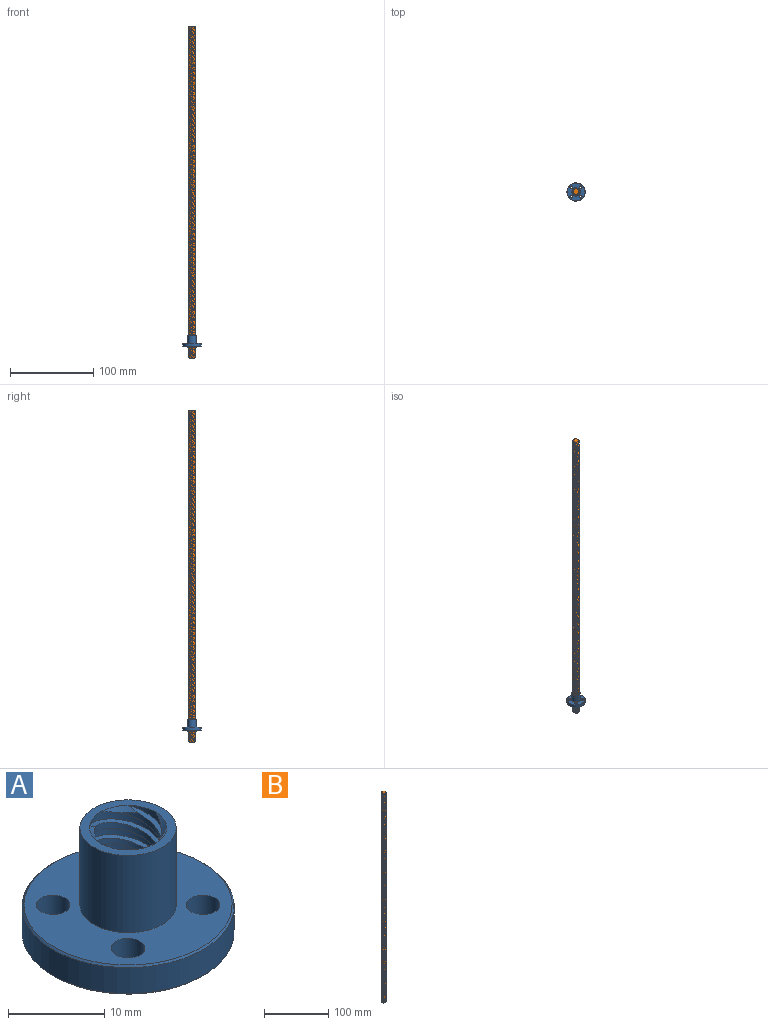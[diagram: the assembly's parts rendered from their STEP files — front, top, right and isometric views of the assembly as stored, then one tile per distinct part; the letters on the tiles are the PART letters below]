
ASSEMBLY  parts=2 mates=1
PART A: 37 faces, bbox 22x22x17.5 mm
  f0: plane 10x10mm, normal (0,0,-1), area 28.3mm2, adj f9,f11,f15,f19,f23,f29,f30,f31
  f1: plane 10x10mm, normal (0,0,1), area 28.3mm2, adj f10,f11,f15,f19,f23,f33,f34,f35
  f2: cylinder r=1.75mm len=3.7mm, axis (0,0,-1), area 40.7mm2, adj f7,f8
  f3: cylinder r=1.75mm len=3.7mm, axis (0,0,-1), area 40.7mm2, adj f7,f8
  f4: cylinder r=1.75mm len=3.7mm, axis (0,0,-1), area 40.7mm2, adj f7,f8
  f5: cylinder r=1.75mm len=3.7mm, axis (0,0,-1), area 40.7mm2, adj f7,f8
  f6: cylinder r=11mm len=22mm, axis (0,0,-1), area 228.1mm2, adj f27,f28
  f7: plane 21.6x21.6mm, normal (0,0,1), area 249.4mm2, adj f2,f3,f4,f5,f10,f28
  f8: plane 21.6x21.6mm, normal (0,0,-1), area 249.4mm2, adj f2,f3,f4,f5,f9,f27
  f9: cylinder r=5mm len=10mm, axis (0,0,-1), area 47.1mm2, adj f0,f8
  f10: cylinder r=5mm len=10mm, axis (0,0,-1), area 307.9mm2, adj f1,f7
  f11: cylinder r=4mm len=15mm, axis (0,0,-1), area 47.1mm2, adj f0,f1,f14,f26
  f12: bspline ~16.4x9mm, area 23.4mm2, adj f13,f15,f30,f36
  f13: cylinder r=3.5mm len=14mm, axis (0,0,1), area 28.2mm2, adj f12,f14,f30,f36
  f14: bspline ~17.4x9mm, area 23.4mm2, adj f11,f13,f30,f36
  f15: cylinder r=4mm len=15mm, axis (0,0,-1), area 47.1mm2, adj f0,f1,f12,f18
  f16: bspline ~16.4x9mm, area 23.4mm2, adj f17,f19,f29,f35
  f17: cylinder r=3.5mm len=14mm, axis (0,0,1), area 28.2mm2, adj f16,f18,f29,f35
  f18: bspline ~17.4x9mm, area 23.4mm2, adj f15,f17,f29,f35
  f19: cylinder r=4mm len=15mm, axis (0,0,-1), area 47.1mm2, adj f0,f1,f16,f22
  f20: bspline ~16.4x9mm, area 23.4mm2, adj f21,f23,f32,f34
  f21: cylinder r=3.5mm len=14mm, axis (0,0,1), area 28.2mm2, adj f20,f22,f32,f34
  f22: bspline ~17.4x9mm, area 23.4mm2, adj f19,f21,f32,f34
  f23: cylinder r=4mm len=15mm, axis (0,0,-1), area 47.1mm2, adj f0,f1,f20,f24
  f24: bspline ~17.4x9mm, area 23.4mm2, adj f23,f25,f31,f33
  f25: cylinder r=3.5mm len=14mm, axis (0,0,1), area 28.2mm2, adj f24,f26,f31,f33
  f26: bspline ~16.4x9mm, area 23.4mm2, adj f11,f25,f31,f33
  f27: cone r=11mm half-angle=45deg, axis (0,0,1), area 19.4mm2, adj f6,f8
  f28: cone r=10.8mm half-angle=45deg, axis (0,0,-1), area 19.4mm2, adj f6,f7
  f29: cone r=3.5mm half-angle=45deg, axis (0,0,-1), area 1.8mm2, adj f0,f16,f17,f18
  f30: cone r=3.5mm half-angle=45deg, axis (0,0,-1), area 1.8mm2, adj f0,f12,f13,f14
  f31: cone r=3.5mm half-angle=45deg, axis (0,0,-1), area 1.8mm2, adj f0,f24,f25,f26
  f32: cone r=3.5mm half-angle=45deg, axis (0,0,-1), area 1.8mm2, adj f0,f20,f21,f22
  f33: cone r=4mm half-angle=45deg, axis (0,0,1), area 1.8mm2, adj f1,f24,f25,f26
  f34: cone r=4mm half-angle=45deg, axis (0,0,1), area 1.8mm2, adj f1,f20,f21,f22
  f35: cone r=4mm half-angle=45deg, axis (0,0,1), area 1.8mm2, adj f1,f16,f17,f18
  f36: cone r=4mm half-angle=45deg, axis (0,0,1), area 1.8mm2, adj f1,f12,f13,f14
PART B: 26 faces, bbox 2755.3x2755.3x1138.6 mm
  f0: cylinder r=4mm len=399mm, axis (0,0,-1), area 1245.2mm2, adj f1,f4,f8,f9
  f1: cone r=4mm half-angle=45deg, axis (0,0,1), area 2.4mm2, adj f0,f4,f9,f20
  f2: cone r=3.5mm half-angle=45deg, axis (0,0,-1), area 2.4mm2, adj f3,f18,f19,f23
  f3: bspline ~1382.16x769.95mm, area 643.9mm2, adj f2,f5,f18,f25
  f4: bspline ~1382.16x769.95mm, area 639.5mm2, adj f0,f1,f5,f8
  f5: cylinder r=3.5mm len=400mm, axis (0,0,1), area 862.4mm2, adj f3,f4,f19,f20
  f6: cylinder r=4mm len=399mm, axis (0,0,-1), area 1245.2mm2, adj f7,f10,f14,f15
  f7: cone r=4mm half-angle=45deg, axis (0,0,1), area 2.4mm2, adj f6,f10,f15,f20
  f8: cone r=3.5mm half-angle=45deg, axis (0,0,-1), area 2.4mm2, adj f0,f4,f9,f19
  f9: bspline ~1382.16x769.95mm, area 643.9mm2, adj f0,f1,f8,f11
  f10: bspline ~1382.16x769.95mm, area 639.5mm2, adj f6,f7,f11,f14
  f11: cylinder r=3.5mm len=400mm, axis (0,0,1), area 862.4mm2, adj f9,f10,f19,f20
  f12: cylinder r=4mm len=399mm, axis (0,0,-1), area 1245.2mm2, adj f13,f16,f22,f24
  f13: cone r=4mm half-angle=45deg, axis (0,0,1), area 2.4mm2, adj f12,f16,f20,f22
  f14: cone r=3.5mm half-angle=45deg, axis (0,0,-1), area 2.4mm2, adj f6,f10,f15,f19
  f15: bspline ~1382.16x769.95mm, area 643.9mm2, adj f6,f7,f14,f17
  f16: bspline ~1382.16x769.95mm, area 639.5mm2, adj f12,f13,f17,f24
  f17: cylinder r=3.5mm len=400mm, axis (0,0,1), area 862.4mm2, adj f15,f16,f19,f20
  f18: cylinder r=4mm len=399mm, axis (0,0,-1), area 1245.2mm2, adj f2,f3,f23,f25
  f19: plane 7x7mm, normal (0,0,1), area 38.5mm2, adj f2,f5,f8,f11,f14,f17,f21,f24
  f20: plane 7x7mm, normal (0,0,-1), area 38.5mm2, adj f1,f5,f7,f11,f13,f17,f21,f25
  f21: cylinder r=3.5mm len=400mm, axis (0,0,1), area 862.4mm2, adj f19,f20,f22,f23
  f22: bspline ~1382.16x769.95mm, area 643.9mm2, adj f12,f13,f21,f24
  f23: bspline ~1382.16x769.95mm, area 639.5mm2, adj f2,f18,f21,f25
  f24: cone r=3.5mm half-angle=45deg, axis (0,0,-1), area 2.4mm2, adj f12,f16,f19,f22
  f25: cone r=4mm half-angle=45deg, axis (0,0,1), area 2.4mm2, adj f3,f18,f20,f23
PLACE A t=(0,0,-6.5)mm fixed
PLACE B rot(axis=(0,0,-1),92.3deg) t=(0,0,-12.45)mm
MATE cylindrical B.f0 <-> A.f6  axis (0,0,-1) through (0,0,-12.45)mm
